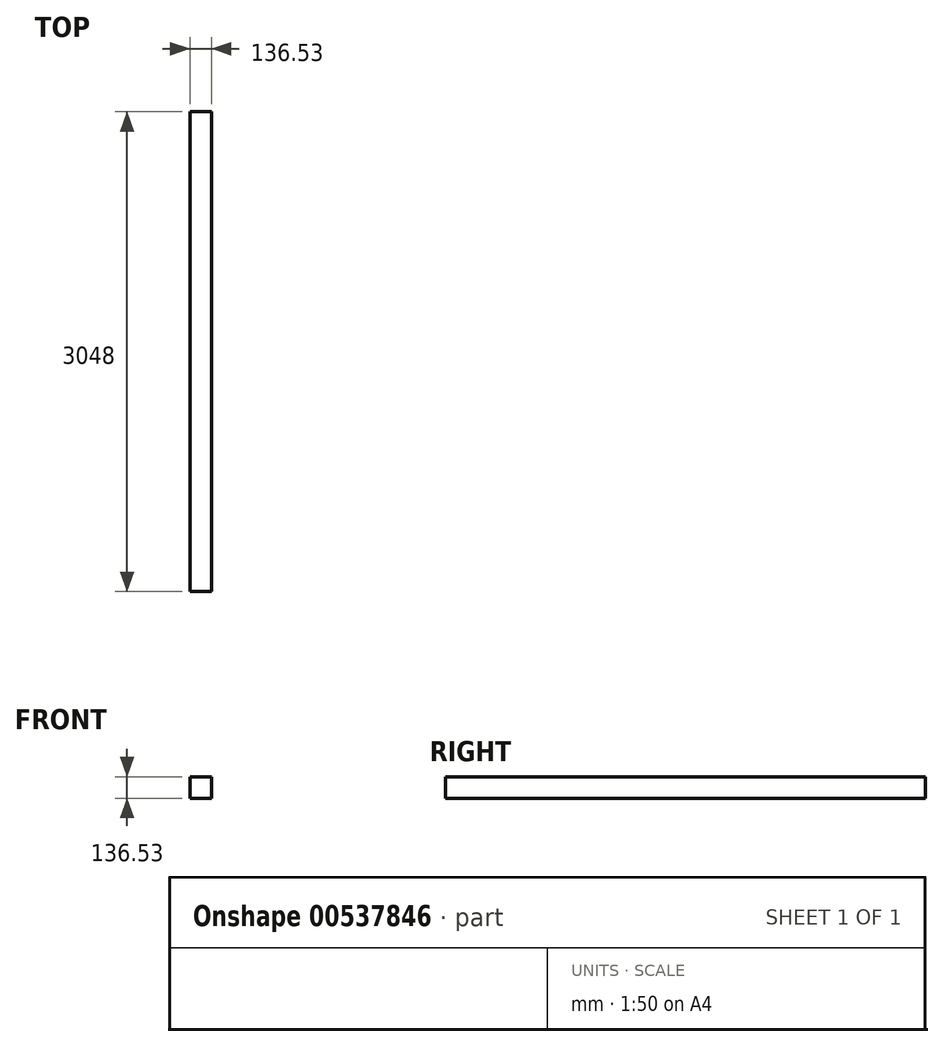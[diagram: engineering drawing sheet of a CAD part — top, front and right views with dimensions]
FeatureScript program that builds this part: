
annotation { "Feature Type Name" : "Feature", "Feature Type Description" : "" }
export const myFeature = defineFeature(function(context is Context, id is Id, definition is map)
    precondition{}
    {
        {
            var Q0;
            Q0=qCreatedBy(makeId("Top.planeOp"),FACE);
            var sketch = newSketch(context, id + "F0", { "sketchPlane" : qUnion([Q0])});
            skLineSegment(sketch, "E0.bottom", {"start": v(-80.75, 2402.86) * mm, "end": v(55.78, 2402.86) * mm});
            skLineSegment(sketch, "E0.top", {"start": v(-80.75, -645.14) * mm, "end": v(55.78, -645.14) * mm});
            skLineSegment(sketch, "E0.left", {"start": v(-80.75, 2402.86) * mm, "end": v(-80.75, -645.14) * mm});
            skLineSegment(sketch, "E0.right", {"start": v(55.78, 2402.86) * mm, "end": v(55.78, -645.14) * mm});
            skSolve(sketch);
        }
        {
            var Q0;
            Q0=makeQuery(id+"F0.imprint","IMPRINT",FACE,{"disambiguationData":[TD([[makeQuery(id+"F0.imprint","IMPRINT",EDGE,{"derivedFrom":sQuery(id+"F0.wireOp",EDGE,"E0.bottom")}),-1.0]])]});
            extrude(context, id + "F1", {"entities" : qUnion([Q0]), "depth" : 136.53 * mm, "offsetDistance" : 25.4 * mm});
        }
    });
